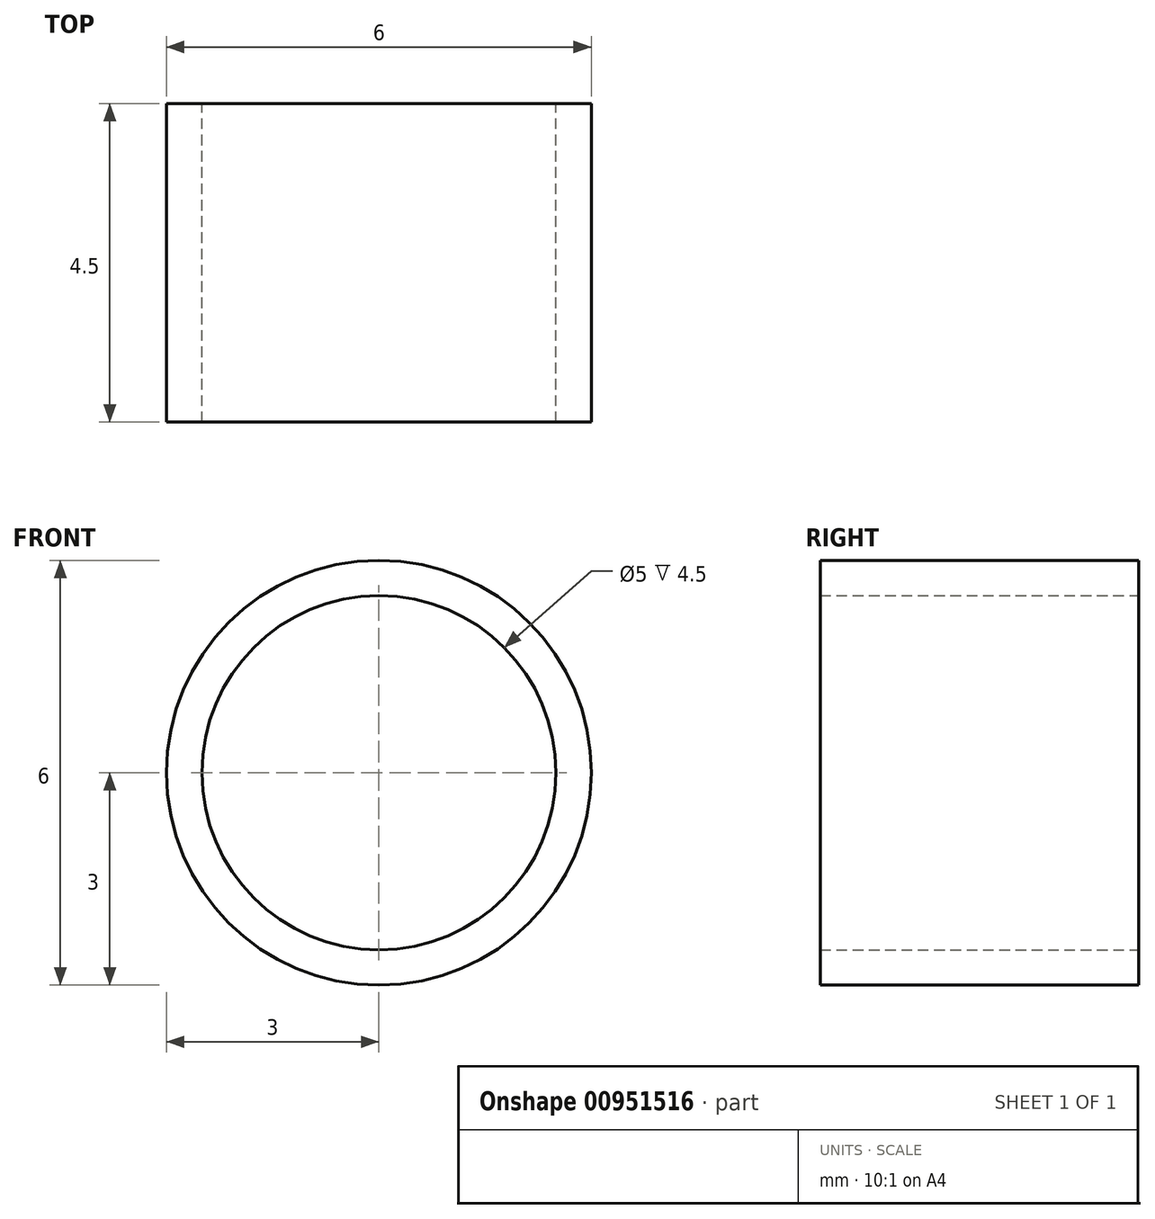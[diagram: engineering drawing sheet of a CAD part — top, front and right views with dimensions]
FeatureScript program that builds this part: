
annotation { "Feature Type Name" : "Feature", "Feature Type Description" : "" }
export const myFeature = defineFeature(function(context is Context, id is Id, definition is map)
    precondition{}
    {
        {
            var Q0;
            Q0=qCreatedBy(makeId("Front.planeOp"),FACE);
            var sketch = newSketch(context, id + "F0", { "sketchPlane" : qUnion([Q0])});
            skCircle(sketch, "E0", {"center": v(0, 0) * mm, "radius": 2.5 * mm});
            skCircle(sketch, "E1", {"center": v(0, 0) * mm, "radius": 3 * mm});
            skSolve(sketch);
        }
        {
            var Q0;
            Q0=makeQuery(id+"F0.imprint","IMPRINT",FACE,{"disambiguationData":[TD([[makeQuery(id+"F0.imprint","IMPRINT",EDGE,{"derivedFrom":sQuery(id+"F0.wireOp",EDGE,"E0")}),-1.0]])]});
            extrude(context, id + "F1", {"entities" : qUnion([Q0]), "depth" : 4.5 * mm, "offsetDistance" : 25 * mm});
        }
    });
